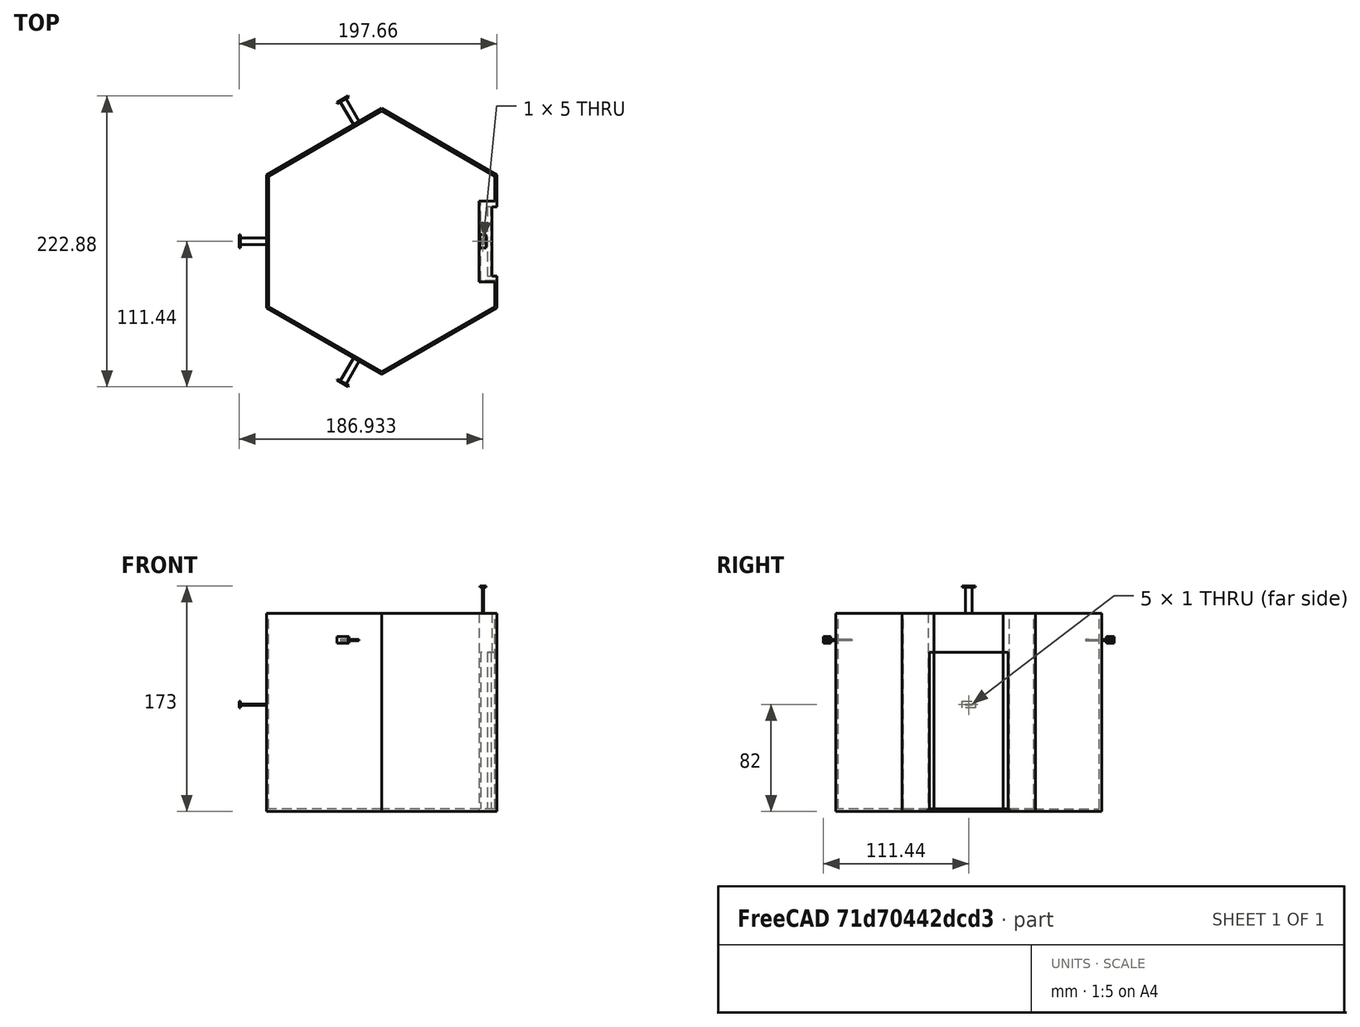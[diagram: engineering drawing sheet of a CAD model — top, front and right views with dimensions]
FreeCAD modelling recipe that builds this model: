
FCSTD DOCUMENT  (FreeCAD 0.20R29177 +426 (Git))
Label: classifier_part
License: All rights reserved
LicenseURL: http://en.wikipedia.org/wiki/All_rights_reserved
objects: Sketcher::SketchObject×14, PartDesign::Pad×12, PartDesign::Pocket×2, PartDesign::CoordinateSystem×1, PartDesign::Body×1
note: 44 computed .brp shape members not serialized (recipe doc carries the construction recipe); baked Part::Feature solids carry a one-line shape summary decoded from their .brp

FEATURE [Sketcher::SketchObject] Sketch007
  FullyConstrained = true
  MapMode = 5
  Support = -> [XY_Plane]
  sketch-geometry (14):
    g0: LineSegment StartX=86.6025 StartY=50 StartZ=0 EndX=1.42e-14 EndY=100 EndZ=0
    g1: LineSegment StartX=1.42e-14 StartY=100 StartZ=0 EndX=-86.6025 EndY=50 EndZ=0
    g2: LineSegment StartX=-86.6025 StartY=50 StartZ=0 EndX=-86.6025 EndY=-50 EndZ=0
    g3: LineSegment StartX=-86.6025 StartY=-50 StartZ=0 EndX=0 EndY=-100 EndZ=0
    g4: LineSegment StartX=0 StartY=-100 StartZ=0 EndX=86.6025 EndY=-50 EndZ=0
    g5: LineSegment StartX=86.6025 StartY=-50 StartZ=0 EndX=86.6025 EndY=50 EndZ=0
    g6: Circle CenterX=0 CenterY=0 CenterZ=0 NormalX=0 NormalY=0 NormalZ=1 AngleXU=0 Radius=100
    g7: LineSegment StartX=88.3346 StartY=51 StartZ=0 EndX=0 EndY=102 EndZ=0
    g8: LineSegment StartX=0 StartY=102 StartZ=0 EndX=-88.3346 EndY=51 EndZ=0
    g9: LineSegment StartX=-88.3346 StartY=51 StartZ=0 EndX=-88.3346 EndY=-51 EndZ=0
    g10: LineSegment StartX=-88.3346 StartY=-51 StartZ=0 EndX=1.42e-14 EndY=-102 EndZ=0
    g11: LineSegment StartX=1.42e-14 StartY=-102 StartZ=0 EndX=88.3346 EndY=-51 EndZ=0
    g12: LineSegment StartX=88.3346 StartY=-51 StartZ=0 EndX=88.3346 EndY=51 EndZ=0
    g13: Circle CenterX=0 CenterY=0 CenterZ=0 NormalX=0 NormalY=0 NormalZ=1 AngleXU=0 Radius=102
  constraints (32):
    c: Coincident(g0,g1)
    c: Coincident(g1,g2)
    c: Coincident(g2,g3)
    c: Coincident(g3,g4)
    c: Coincident(g4,g5)
    c: Coincident(g5,g0)
    c: Equal(g0, g1-g5) x5
    c: PointOnObject(g0,g6)
    c: PointOnObject(g1,g6)
    c: PointOnObject(g2,g6)
    c: PointOnObject(g3,g6)
    c: PointOnObject(g4,g6)
    c: PointOnObject(g5,g6)
    c: Coincident(g6,g-1)
    c: PointOnObject(g3,g-2)
    c: DistanceY(g5,g5) = 100
    c: Coincident(g7,g8)
    c: Coincident(g8,g9)
    c: Coincident(g9,g10)
    c: Coincident(g10,g11)
    c: Coincident(g11,g12)
    c: Coincident(g12,g7)
    c: Equal(g7, g8-g12) x5
    c: PointOnObject(g7,g13)
    c: PointOnObject(g8,g13)
    c: PointOnObject(g9,g13)
    c: PointOnObject(g10,g13)
    c: PointOnObject(g11,g13)
    c: PointOnObject(g12,g13)
    c: Coincident(g13,g6)
    c: Distance(g0,g7) = 2
    c: PointOnObject(g7,g-2)
FEATURE [PartDesign::Pad] Pad
  Direction = (0,0,1)
  Length = 150
  Length2 = 10
  Profile = -> Sketch007
  ReferenceAxis = -> Sketch007 [N_Axis]
  Type = 0
FEATURE [Sketcher::SketchObject] Sketch
  ExternalGeometry = -> [Pad]
  FullyConstrained = true
  MapMode = 5
  Placement = pos=(86.6025,-1.21e-14,0) rot=(-0.57735,0.57735,0.57735;4.18879rad)
  Support = -> [Pad]
  sketch-geometry (4):
    g0: LineSegment StartX=-31 StartY=150 StartZ=0 EndX=31 EndY=150 EndZ=0
    g1: LineSegment StartX=31 StartY=150 StartZ=0 EndX=31 EndY=0 EndZ=0
    g2: LineSegment StartX=31 StartY=0 StartZ=0 EndX=-31 EndY=0 EndZ=0
    g3: LineSegment StartX=-31 StartY=0 StartZ=0 EndX=-31 EndY=150 EndZ=0
  constraints (11):
    c: Coincident(g0,g1)
    c: Coincident(g1,g2)
    c: Coincident(g2,g3)
    c: Coincident(g3,g0)
    c: Horizontal(g2)
    c: Vertical(g1)
    c: Vertical(g3)
    c: PointOnObject(g1,g-1)
    c: PointOnObject(g0,g-3)
    c: Symmetric(g0,g0,g-2)
    c: DistanceX(g0,g0) = 62
FEATURE [PartDesign::Pad] Pad001
  BaseFeature = -> Pad
  Direction = (-1,1e-16,1e-16)
  Length = 12
  Length2 = 10
  Profile = -> Sketch
  ReferenceAxis = -> Sketch [N_Axis]
  Type = 0
FEATURE [Sketcher::SketchObject] Sketch008
  FullyConstrained = true
  MapMode = 5
  Placement = pos=(88.3346,0,0) rot=(0.57735,0.57735,0.57735;2.0944rad)
  Support = -> [Pad001]
  sketch-geometry (4):
    g0: LineSegment StartX=-30.25 StartY=120 StartZ=0 EndX=30.25 EndY=120 EndZ=0
    g1: LineSegment StartX=30.25 StartY=120 StartZ=0 EndX=30.25 EndY=0 EndZ=0
    g2: LineSegment StartX=30.25 StartY=0 StartZ=0 EndX=-30.25 EndY=0 EndZ=0
    g3: LineSegment StartX=-30.25 StartY=0 StartZ=0 EndX=-30.25 EndY=120 EndZ=0
  constraints (11):
    c: Coincident(g0,g1)
    c: Coincident(g1,g2)
    c: Coincident(g2,g3)
    c: Coincident(g3,g0)
    c: Horizontal(g0)
    c: Vertical(g1)
    c: Vertical(g3)
    c: PointOnObject(g1,g-1)
    c: Symmetric(g1,g2,g-2)
    c: DistanceX(g2,g1) = 60.5
    c: DistanceY(g1,g1) = 120
FEATURE [PartDesign::Pocket] Pocket
  BaseFeature = -> Pad001
  Direction = (-1,0,0)
  Length = 12.5
  Length2 = 5
  Profile = -> Sketch008
  ReferenceAxis = -> Sketch008 [N_Axis]
  Type = 0
FEATURE [Sketcher::SketchObject] Sketch009
  ExternalGeometry = -> [Pocket]
  FullyConstrained = true
  MapMode = 5
  Placement = pos=(0,0,120) rot=(1,0,0;3.14159rad)
  Support = -> [Pocket]
  sketch-geometry (4):
    g0: LineSegment StartX=80.8346 StartY=26.5 StartZ=0 EndX=83.8346 EndY=26.5 EndZ=0
    g1: LineSegment StartX=83.8346 StartY=26.5 StartZ=0 EndX=83.8346 EndY=-26.5 EndZ=0
    g2: LineSegment StartX=83.8346 StartY=-26.5 StartZ=0 EndX=80.8346 EndY=-26.5 EndZ=0
    g3: LineSegment StartX=80.8346 StartY=-26.5 StartZ=0 EndX=80.8346 EndY=26.5 EndZ=0
  constraints (12):
    c: Coincident(g0,g1)
    c: Coincident(g1,g2)
    c: Coincident(g2,g3)
    c: Coincident(g3,g0)
    c: Horizontal(g0)
    c: Horizontal(g2)
    c: Vertical(g3)
    c: DistanceY(g1,g1) = 53
    c: DistanceX(g2,g2) = 3
    c: Symmetric(g1,g0,g-1)
    c: DistanceX(g-5,g2) = 5
    c: DistanceX(g1,g-3) = 4.5
FEATURE [PartDesign::Pad] Pad002  label="connectorPad"
  BaseFeature = -> Pocket
  Direction = (0,0,-1)
  Length = 120
  Length2 = 10
  Profile = -> Sketch009
  ReferenceAxis = -> Sketch009 [N_Axis]
  Type = 0
FEATURE [Sketcher::SketchObject] Sketch010
  ExternalGeometry = -> [Pad002]
  FullyConstrained = true
  MapMode = 5
  Placement = pos=(-44.1673,76.5,0) rot=(-0.186157,0.694747,0.694747;3.50969rad)
  Support = -> [Pad002]
  sketch-geometry (4):
    g0: LineSegment StartX=-31 StartY=130 StartZ=0 EndX=-26 EndY=130 EndZ=0
    g1: LineSegment StartX=-26 StartY=130 StartZ=0 EndX=-26 EndY=129 EndZ=0
    g2: LineSegment StartX=-26 StartY=129 StartZ=0 EndX=-31 EndY=129 EndZ=0
    g3: LineSegment StartX=-31 StartY=129 StartZ=0 EndX=-31 EndY=130 EndZ=0
  constraints (12):
    c: Coincident(g0,g1)
    c: Coincident(g1,g2)
    c: Coincident(g2,g3)
    c: Coincident(g3,g0)
    c: Horizontal(g0)
    c: Horizontal(g2)
    c: Vertical(g1)
    c: Vertical(g3)
    c: DistanceY(g0,g-4) = 20
    c: DistanceX(g-4,g0) = 20
    c: DistanceX(g0,g0) = 5
    c: DistanceY(g1,g1) = 1
FEATURE [PartDesign::Pad] Pad003
  BaseFeature = -> Pad002
  Direction = (-0.5,0.866025,1e-16)
  Length = 20
  Length2 = 10
  Profile = -> Sketch010
  ReferenceAxis = -> Sketch010 [N_Axis]
  Type = 0
FEATURE [Sketcher::SketchObject] Sketch011
  ExternalGeometry = -> [Pad003]
  FullyConstrained = true
  MapMode = 5
  Placement = pos=(-54.1673,93.8205,1.972e-13) rot=(-0.186157,0.694747,0.694747;3.50969rad)
  Support = -> [Pad003]
  sketch-geometry (6):
    g0: LineSegment StartX=-33.5 StartY=132 StartZ=0 EndX=-33.5 EndY=127 EndZ=0
    g1: LineSegment StartX=-33.5 StartY=127 StartZ=0 EndX=-23.5 EndY=127 EndZ=0
    g2: LineSegment StartX=-23.5 StartY=127 StartZ=0 EndX=-23.5 EndY=132 EndZ=0
    g3: LineSegment StartX=-23.5 StartY=132 StartZ=0 EndX=-33.5 EndY=132 EndZ=0
    g4: GeomPoint X=-28.5 Y=129.5 Z=0
    g5: GeomPoint X=-28.5 Y=129.5 Z=0
  constraints (13):
    c: Coincident(g0,g1)
    c: Coincident(g1,g2)
    c: Coincident(g2,g3)
    c: Coincident(g3,g0)
    c: Horizontal(g1)
    c: Horizontal(g3)
    c: Vertical(g0)
    c: Vertical(g2)
    c: Symmetric(g1,g0,g4)
    c: Symmetric(g-3,g-4,g5)
    c: Coincident(g4,g5)
    c: DistanceY(g2,g2) = 5
    c: DistanceX(g1,g1) = 10
FEATURE [PartDesign::Pad] Pad004
  BaseFeature = -> Pad003
  Direction = (-0.5,0.866025,1.5e-15)
  Length = 1
  Length2 = 10
  Profile = -> Sketch011
  ReferenceAxis = -> Sketch011 [N_Axis]
  Type = 0
FEATURE [Sketcher::SketchObject] Sketch012
  ExternalGeometry = -> [Pad004]
  FullyConstrained = true
  MapMode = 5
  Placement = pos=(-44.1673,-76.5,0) rot=(0.935113,-0.250563,-0.250563;1.63783rad)
  Support = -> [Pad004]
  sketch-geometry (5):
    g0: LineSegment StartX=26 StartY=130 StartZ=0 EndX=26 EndY=129 EndZ=0
    g1: LineSegment StartX=26 StartY=129 StartZ=0 EndX=31 EndY=129 EndZ=0
    g2: LineSegment StartX=31 StartY=129 StartZ=0 EndX=31 EndY=130 EndZ=0
    g3: LineSegment StartX=31 StartY=130 StartZ=0 EndX=26 EndY=130 EndZ=0
    g4: GeomPoint X=28.5 Y=129.5 Z=0
  constraints (13):
    c: Coincident(g0,g1)
    c: Coincident(g1,g2)
    c: Coincident(g2,g3)
    c: Coincident(g3,g0)
    c: Horizontal(g1)
    c: Horizontal(g3)
    c: Vertical(g0)
    c: Vertical(g2)
    c: Symmetric(g1,g0,g4)
    c: DistanceY(g2,g-4) = 20
    c: DistanceX(g2,g-4) = 20
    c: DistanceY(g2,g2) = 1
    c: DistanceX(g1,g1) = 5
FEATURE [PartDesign::Pad] Pad005
  BaseFeature = -> Pad004
  Direction = (-0.5,-0.866025,-1e-16)
  Length = 20
  Length2 = 10
  Profile = -> Sketch012
  ReferenceAxis = -> Sketch012 [N_Axis]
  Type = 0
FEATURE [Sketcher::SketchObject] Sketch013
  ExternalGeometry = -> [Pad005]
  FullyConstrained = true
  MapMode = 5
  Placement = pos=(-54.1673,-93.8205,-2.004e-13) rot=(0.935113,-0.250563,-0.250563;1.63783rad)
  Support = -> [Pad005]
  sketch-geometry (6):
    g0: LineSegment StartX=23.5 StartY=132 StartZ=0 EndX=23.5 EndY=127 EndZ=0
    g1: LineSegment StartX=23.5 StartY=127 StartZ=0 EndX=33.5 EndY=127 EndZ=0
    g2: LineSegment StartX=33.5 StartY=127 StartZ=0 EndX=33.5 EndY=132 EndZ=0
    g3: LineSegment StartX=33.5 StartY=132 StartZ=0 EndX=23.5 EndY=132 EndZ=0
    g4: GeomPoint X=28.5 Y=129.5 Z=0
    g5: GeomPoint X=28.5 Y=129.5 Z=0
  constraints (13):
    c: Coincident(g0,g1)
    c: Coincident(g1,g2)
    c: Coincident(g2,g3)
    c: Coincident(g3,g0)
    c: Horizontal(g1)
    c: Horizontal(g3)
    c: Vertical(g0)
    c: Vertical(g2)
    c: Symmetric(g1,g0,g4)
    c: Symmetric(g-4,g-3,g5)
    c: Coincident(g4,g5)
    c: DistanceX(g1,g1) = 10
    c: DistanceY(g2,g2) = 5
FEATURE [PartDesign::Pad] Pad006
  BaseFeature = -> Pad005
  Direction = (-0.5,-0.866025,-1.9e-15)
  Length = 1
  Length2 = 10
  Profile = -> Sketch013
  ReferenceAxis = -> Sketch013 [N_Axis]
  Type = 0
FEATURE [Sketcher::SketchObject] Sketch014
  ExternalGeometry = -> [Pad006]
  FullyConstrained = true
  MapMode = 5
  Placement = pos=(1.65e-14,-1.65e-14,150) rot=(0,0,1;0rad)
  Support = -> [Pad006]
  sketch-geometry (6):
    g0: LineSegment StartX=77.1025 StartY=-2.5 StartZ=0 EndX=77.1025 EndY=2.5 EndZ=0
    g1: LineSegment StartX=77.1025 StartY=2.5 StartZ=0 EndX=78.1025 EndY=2.5 EndZ=0
    g2: LineSegment StartX=78.1025 StartY=2.5 StartZ=0 EndX=78.1025 EndY=-2.5 EndZ=0
    g3: LineSegment StartX=78.1025 StartY=-2.5 StartZ=0 EndX=77.1025 EndY=-2.5 EndZ=0
    g4: GeomPoint X=77.6025 Y=0 Z=0
    g5: GeomPoint X=86.6025 Y=0 Z=0
  constraints (15):
    c: Coincident(g0,g1)
    c: Coincident(g1,g2)
    c: Coincident(g2,g3)
    c: Coincident(g3,g0)
    c: Horizontal(g1)
    c: Horizontal(g3)
    c: Vertical(g0)
    c: Vertical(g2)
    c: Symmetric(g1,g0,g4)
    c: PointOnObject(g4,g-1)
    c: DistanceY(g2,g2) = 5
    c: DistanceX(g1,g1) = 1
    c: PointOnObject(g5,g-3)
    c: PointOnObject(g5,g-1)
    c: DistanceX(g4,g5) = 9
FEATURE [PartDesign::Pad] Pad007
  BaseFeature = -> Pad006
  Direction = (1e-16,-1e-16,1)
  Length = 20
  Length2 = 10
  Profile = -> Sketch014
  ReferenceAxis = -> Sketch014 [N_Axis]
  Type = 0
FEATURE [Sketcher::SketchObject] Sketch015
  ExternalGeometry = -> [Pad007]
  FullyConstrained = true
  MapMode = 5
  Placement = pos=(0,0,170) rot=(0,0,1;0rad)
  Support = -> [Pad007]
  sketch-geometry (6):
    g0: GeomPoint X=77.6025 Y=-2.11e-14 Z=0
    g1: LineSegment StartX=75.1025 StartY=5 StartZ=0 EndX=75.1025 EndY=-5 EndZ=0
    g2: LineSegment StartX=75.1025 StartY=-5 StartZ=0 EndX=80.1025 EndY=-5 EndZ=0
    g3: LineSegment StartX=80.1025 StartY=-5 StartZ=0 EndX=80.1025 EndY=5 EndZ=0
    g4: LineSegment StartX=80.1025 StartY=5 StartZ=0 EndX=75.1025 EndY=5 EndZ=0
    g5: GeomPoint X=77.6025 Y=-2.11e-14 Z=0
  constraints (13):
    c: Symmetric(g-3,g-4,g0)
    c: Coincident(g1,g2)
    c: Coincident(g2,g3)
    c: Coincident(g3,g4)
    c: Coincident(g4,g1)
    c: Horizontal(g2)
    c: Horizontal(g4)
    c: Vertical(g1)
    c: Vertical(g3)
    c: Symmetric(g2,g1,g5)
    c: Coincident(g5,g0)
    c: DistanceX(g2,g2) = 5
    c: DistanceY(g3,g3) = 10
FEATURE [PartDesign::Pad] Pad008
  BaseFeature = -> Pad007
  Direction = (0,0,1)
  Length = 1
  Length2 = 10
  Profile = -> Sketch015
  ReferenceAxis = -> Sketch015 [N_Axis]
  Type = 0
FEATURE [Sketcher::SketchObject] Sketch016
  FullyConstrained = false
  MapMode = 5
  Placement = pos=(-88.3346,-1.24e-14,0) rot=(0.57735,-0.57735,-0.57735;2.0944rad)
  Support = -> [Pad008]
  sketch-geometry (6):
    g0: LineSegment StartX=-2.5 StartY=80.5 StartZ=0 EndX=-2.5 EndY=79.5 EndZ=0
    g1: LineSegment StartX=-2.5 StartY=79.5 StartZ=0 EndX=2.5 EndY=79.5 EndZ=0
    g2: LineSegment StartX=2.5 StartY=79.5 StartZ=0 EndX=2.5 EndY=80.5 EndZ=0
    g3: LineSegment StartX=2.5 StartY=80.5 StartZ=0 EndX=-2.5 EndY=80.5 EndZ=0
    g4: GeomPoint X=0 Y=80 Z=0
    g5: GeomPoint X=0 Y=150 Z=0
  constraints (14):
    c: Coincident(g0,g1)
    c: Coincident(g1,g2)
    c: Coincident(g2,g3)
    c: Coincident(g3,g0)
    c: Horizontal(g1)
    c: Horizontal(g3)
    c: Vertical(g0)
    c: Vertical(g2)
    c: Symmetric(g1,g0,g4)
    c: PointOnObject(g4,g-2)
    c: DistanceX(g1,g1) = 5
    c: DistanceY(g2,g2) = 1
    c: PointOnObject(g5,g-2)
    c: DistanceY(g4,g5) = 70
FEATURE [PartDesign::Pad] Pad009
  BaseFeature = -> Pad008
  Direction = (-1,-1e-16,-1e-16)
  Length = 20
  Length2 = 10
  Profile = -> Sketch016
  ReferenceAxis = -> Sketch016 [N_Axis]
  Type = 0
FEATURE [Sketcher::SketchObject] Sketch017
  ExternalGeometry = -> [Pad009]
  FullyConstrained = true
  MapMode = 5
  Placement = pos=(-108.335,0,0) rot=(0.57735,-0.57735,-0.57735;2.0944rad)
  Support = -> [Pad009]
  sketch-geometry (7):
    g0: LineSegment StartX=-5 StartY=82.5 StartZ=0 EndX=-5 EndY=77.5 EndZ=0
    g1: LineSegment StartX=-5 StartY=77.5 StartZ=0 EndX=5 EndY=77.5 EndZ=0
    g2: LineSegment StartX=5 StartY=77.5 StartZ=0 EndX=5 EndY=82.5 EndZ=0
    g3: LineSegment StartX=5 StartY=82.5 StartZ=0 EndX=-5 EndY=82.5 EndZ=0
    g4: GeomPoint X=2.27e-14 Y=80 Z=0
    g5: GeomPoint X=2.27e-14 Y=80 Z=0
    g6: GeomPoint X=2.27e-14 Y=80 Z=0
  constraints (14):
    c: Coincident(g0,g1)
    c: Coincident(g1,g2)
    c: Coincident(g2,g3)
    c: Coincident(g3,g0)
    c: Horizontal(g1)
    c: Horizontal(g3)
    c: Vertical(g0)
    c: Vertical(g2)
    c: Symmetric(g1,g0,g4)
    c: Coincident(g4,g5)
    c: DistanceX(g1,g1) = 10
    c: DistanceY(g2,g2) = 5
    c: Symmetric(g-4,g-3,g6)
    c: Coincident(g4,g6)
FEATURE [PartDesign::Pad] Pad010
  BaseFeature = -> Pad009
  Direction = (-1,0,0)
  Length = 1
  Length2 = 10
  Profile = -> Sketch017
  ReferenceAxis = -> Sketch017 [N_Axis]
  Type = 0
FEATURE [Sketcher::SketchObject] Sketch018
  ExternalGeometry = -> [Pad010]
  FullyConstrained = true
  MapMode = 5
  Placement = pos=(1.65e-14,-1.65e-14,150) rot=(0,0,1;0rad)
  Support = -> [Pad010]
  sketch-geometry (4):
    g0: LineSegment StartX=84.3346 StartY=26.5 StartZ=0 EndX=88.3346 EndY=26.5 EndZ=0
    g1: LineSegment StartX=88.3346 StartY=26.5 StartZ=0 EndX=88.3346 EndY=-26.5 EndZ=0
    g2: LineSegment StartX=88.3346 StartY=-26.5 StartZ=0 EndX=84.3346 EndY=-26.5 EndZ=0
    g3: LineSegment StartX=84.3346 StartY=-26.5 StartZ=0 EndX=84.3346 EndY=26.5 EndZ=0
  constraints (12):
    c: Coincident(g0,g1)
    c: Coincident(g1,g2)
    c: Coincident(g2,g3)
    c: Coincident(g3,g0)
    c: Horizontal(g0)
    c: Horizontal(g2)
    c: Vertical(g3)
    c: DistanceY(g1,g1) = 53
    c: Symmetric(g0,g1,g-1)
    c: Tangent(g1,g-3)
    c: Tangent(g1,g-3) = 1.5708
    c: DistanceX(g2,g2) = 4
FEATURE [PartDesign::CoordinateSystem] LCS_1
  AttacherType = Attacher::AttachEngine3D
  AttachmentOffset = pos=(0,0,0) rot=(-1,0,0;1.5708rad)
  MapMode = 45
  Placement = pos=(83.8346,1.8e-15,120) rot=(0,0,1;3.14159rad)
  Support = -> [Pad010]
FEATURE [PartDesign::Pocket] Pocket001
  BaseFeature = -> Pad010
  Direction = (-1e-16,1e-16,-1)
  Length = 30
  Length2 = 5
  Profile = -> Sketch018
  ReferenceAxis = -> Sketch018 [N_Axis]
  Type = 0
FEATURE [Sketcher::SketchObject] Sketch019
  ExternalGeometry = -> [Pocket001]
  FullyConstrained = true
  MapMode = 5
  Placement = pos=(0,0,0) rot=(1,0,0;3.14159rad)
  Support = -> [Pocket001]
  sketch-geometry (12):
    g0: LineSegment StartX=88.3346 StartY=-51 StartZ=0 EndX=88.3346 EndY=51 EndZ=0
    g1: LineSegment StartX=88.3346 StartY=51 StartZ=0 EndX=-1.42e-14 EndY=102 EndZ=0
    g2: LineSegment StartX=-1.42e-14 StartY=102 StartZ=0 EndX=-88.3346 EndY=51 EndZ=0
    g3: LineSegment StartX=-88.3346 StartY=51 StartZ=0 EndX=-88.3346 EndY=-51 EndZ=0
    g4: LineSegment StartX=-88.3346 StartY=-51 StartZ=0 EndX=0 EndY=-102 EndZ=0
    g5: LineSegment StartX=0 StartY=-102 StartZ=0 EndX=88.3346 EndY=-51 EndZ=0
    g6: Circle CenterX=0 CenterY=0 CenterZ=0 NormalX=0 NormalY=0 NormalZ=1 AngleXU=0 Radius=102
    g7: LineSegment StartX=88.3346 StartY=-31 StartZ=0 EndX=88.3346 EndY=-51 EndZ=0
    g8: LineSegment StartX=88.3346 StartY=-31 StartZ=0 EndX=74.6025 EndY=-31 EndZ=0
    g9: LineSegment StartX=74.6025 StartY=-31 StartZ=0 EndX=74.6025 EndY=31 EndZ=0
    g10: LineSegment StartX=88.3346 StartY=31 StartZ=0 EndX=74.6025 EndY=31 EndZ=0
    g11: LineSegment StartX=88.3346 StartY=51 StartZ=0 EndX=88.3346 EndY=31 EndZ=0
  constraints (27):
    c: Coincident(g0,g1)
    c: Coincident(g1,g2)
    c: Coincident(g2,g3)
    c: Coincident(g3,g4)
    c: Coincident(g4,g5)
    c: Coincident(g5,g0)
    c: Equal(g0, g1-g5) x5
    c: PointOnObject(g0,g6)
    c: PointOnObject(g1,g6)
    c: PointOnObject(g2,g6)
    c: PointOnObject(g3,g6)
    c: PointOnObject(g4,g6)
    c: PointOnObject(g5,g6)
    c: Coincident(g6,g-1)
    c: Coincident(g0,g-3)
    c: PointOnObject(g7,g0)
    c: Coincident(g7,g5)
    c: Coincident(g8,g7)
    c: Coincident(g8,g-5)
    c: Horizontal(g8)
    c: Coincident(g9,g8)
    c: Coincident(g9,g-4)
    c: PointOnObject(g10,g0)
    c: Coincident(g10,g9)
    c: Horizontal(g10)
    c: Coincident(g11,g1)
    c: Coincident(g11,g10)
FEATURE [PartDesign::Pad] Pad011
  BaseFeature = -> Pocket001
  Direction = (0,0,-1)
  Length = 2
  Length2 = 10
  Profile = -> Sketch019
  ReferenceAxis = -> Sketch019 [N_Axis]
  Type = 0
FEATURE [PartDesign::Body] Body  label="ClassifierPartBody"
  Group = -> [Sketch007,Pad,Sketch,Pad001,Sketch008,Pocket,Sketch009,Pad002,Sketch010,Pad003,Sketch011,Pad004,Sketch012,Pad005,Sketch013,Pad006,Sketch014,Pad007,Sketch015,Pad008,Sketch016,Sketch017,Pad009,Pad010,Sketch018,LCS_1,Pocket001,Sketch019,Pad011]
  Origin = -> Origin
  Tip = -> Pad011
